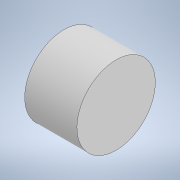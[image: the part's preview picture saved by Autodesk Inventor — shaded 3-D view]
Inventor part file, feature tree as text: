
AUTODESK INVENTOR PART (.ipt)
format: ipt  version: 2020 (Build 240168000, 168)  size: 107,520 bytes
history: native  units: in
note: dims shown in document units (in); Inventor stores cm internally (conversion verified against a paired STEP export)
features: extrude x2, sketch x2
ambient origin geometry x8: Origin, YZ Plane, XZ Plane, XY Plane, X Axis, Y Axis, Z Axis, Center Point
bodies: Solid1 (feature_tree)
feature tree (4):
  extrude  "Extrusion1"  Depth=0.1969in
  extrude  "Extrusion2"  Depth=0.2756in
  sketch  "Sketch1"  dims[d0=0.7087in d1=0.1969in]
  sketch  "Sketch2"  dims[d2=0.0in d4=0.2756in d5=0.0in]
